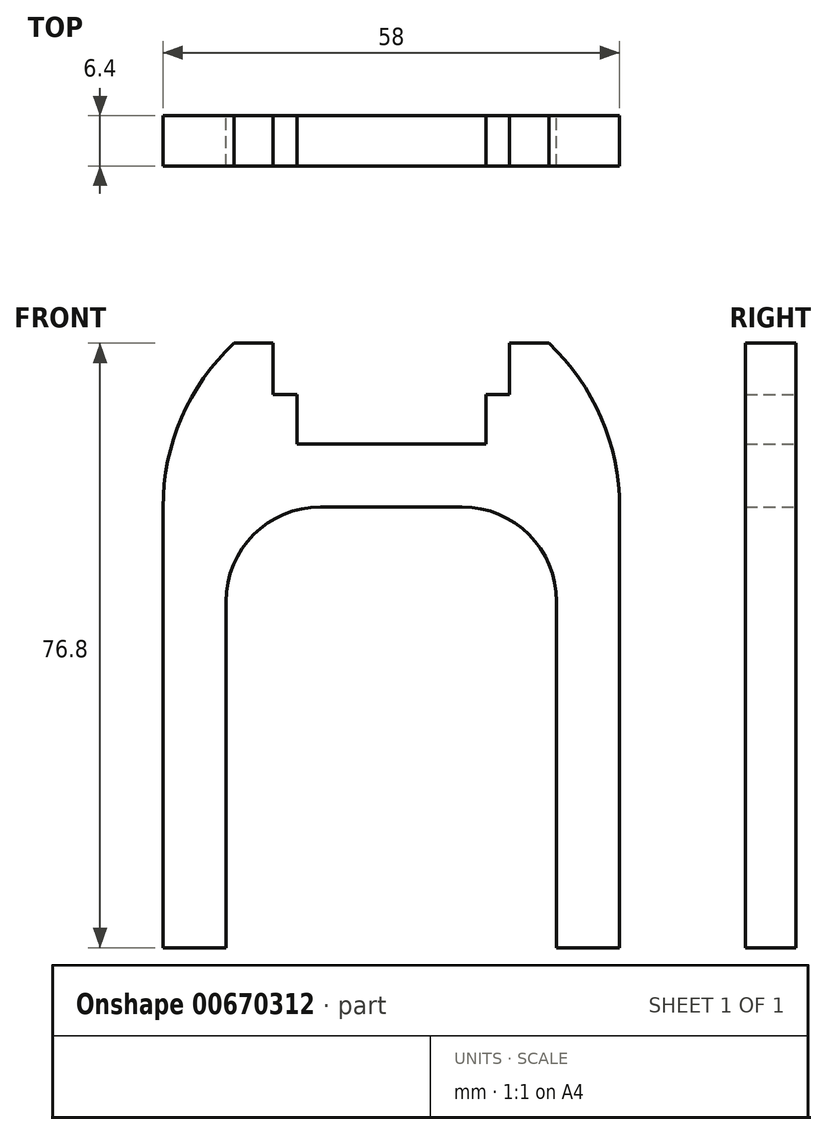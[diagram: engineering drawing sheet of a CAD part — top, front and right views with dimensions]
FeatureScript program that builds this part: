
annotation { "Feature Type Name" : "Feature", "Feature Type Description" : "" }
export const myFeature = defineFeature(function(context is Context, id is Id, definition is map)
    precondition{}
    {
        {
            assignVariable(context, id + "F0", {"name" : "thickness", "anyValue" : 6.4});
        }
        {
            var Q0;
            Q0=qCreatedBy(makeId("Front.planeOp"),FACE);
            var sketch = newSketch(context, id + "F1", { "sketchPlane" : qUnion([Q0])});
            skLineSegment(sketch, "E0", {"start": v(12, 0) * mm, "end": v(-12, 0) * mm});
            skLineSegment(sketch, "E1", {"start": v(-12, 0) * mm, "end": v(-12, 6.3) * mm});
            skLineSegment(sketch, "E2", {"start": v(-12, 6.3) * mm, "end": v(-15, 6.3) * mm});
            skLineSegment(sketch, "E3", {"start": v(-15, 6.3) * mm, "end": v(-15, 12.8) * mm});
            skLineSegment(sketch, "E4", {"start": v(-15, 12.8) * mm, "end": v(-20, 12.8) * mm});
            skLineSegment(sketch, "E5", {"start": v(12, 0) * mm, "end": v(12, 6.3) * mm});
            skLineSegment(sketch, "E6", {"start": v(12, 6.3) * mm, "end": v(15, 6.3) * mm});
            skLineSegment(sketch, "E7", {"start": v(15, 6.3) * mm, "end": v(15, 12.8) * mm});
            skLineSegment(sketch, "E8", {"start": v(15, 12.8) * mm, "end": v(20, 12.8) * mm});
            skLineSegment(sketch, "E9", {"start": v(-29, -8) * mm, "end": v(-29, -64) * mm});
            skLineSegment(sketch, "E10", {"start": v(-29, -64) * mm, "end": v(-21, -64) * mm});
            skLineSegment(sketch, "E11", {"start": v(-21, -64) * mm, "end": v(-21, -20) * mm});
            skLineSegment(sketch, "E12", {"start": v(-9, -8) * mm, "end": v(9, -8) * mm});
            skLineSegment(sketch, "E13", {"start": v(21, -20) * mm, "end": v(21, -64) * mm});
            skLineSegment(sketch, "E14", {"start": v(21, -64) * mm, "end": v(29, -64) * mm});
            skLineSegment(sketch, "E15", {"start": v(29, -64) * mm, "end": v(29, -8) * mm});
            skArc(sketch, "E16", {"start": v(-29, -8) * mm, "mid": v(-26.65, 3.33) * mm, "end": v(-20, 12.8) * mm});
            skArc(sketch, "E17", {"start": v(29, -8) * mm, "mid": v(26.65, 3.33) * mm, "end": v(20, 12.8) * mm});
            skPoint(sketch, "E18.visualSharp", {"position": v(-21, -8) * mm});
            skArc(sketch, "E18.filletArc", {"start": v(-9, -8) * mm, "mid": v(-17.49, -11.51) * mm, "end": v(-21, -20) * mm});
            skPoint(sketch, "E19.visualSharp", {"position": v(21, -8) * mm});
            skArc(sketch, "E19.filletArc", {"start": v(21, -20) * mm, "mid": v(17.49, -11.51) * mm, "end": v(9, -8) * mm});
            skSolve(sketch);
        }
        {
            var Q0;
            Q0=makeQuery(id+"F1.imprint","IMPRINT",FACE,{"disambiguationData":[TD([[makeQuery(id+"F1.imprint","IMPRINT",EDGE,{"derivedFrom":sQuery(id+"F1.wireOp",EDGE,"E0")}),1.0]])]});
            extrude(context, id + "F2", {"entities" : qUnion([Q0]), "endBound" : BoundingType.SYMMETRIC, "depth" : (getVariable(context, 'thickness')) * mm, "offsetDistance" : 25 * mm});
        }
    });
